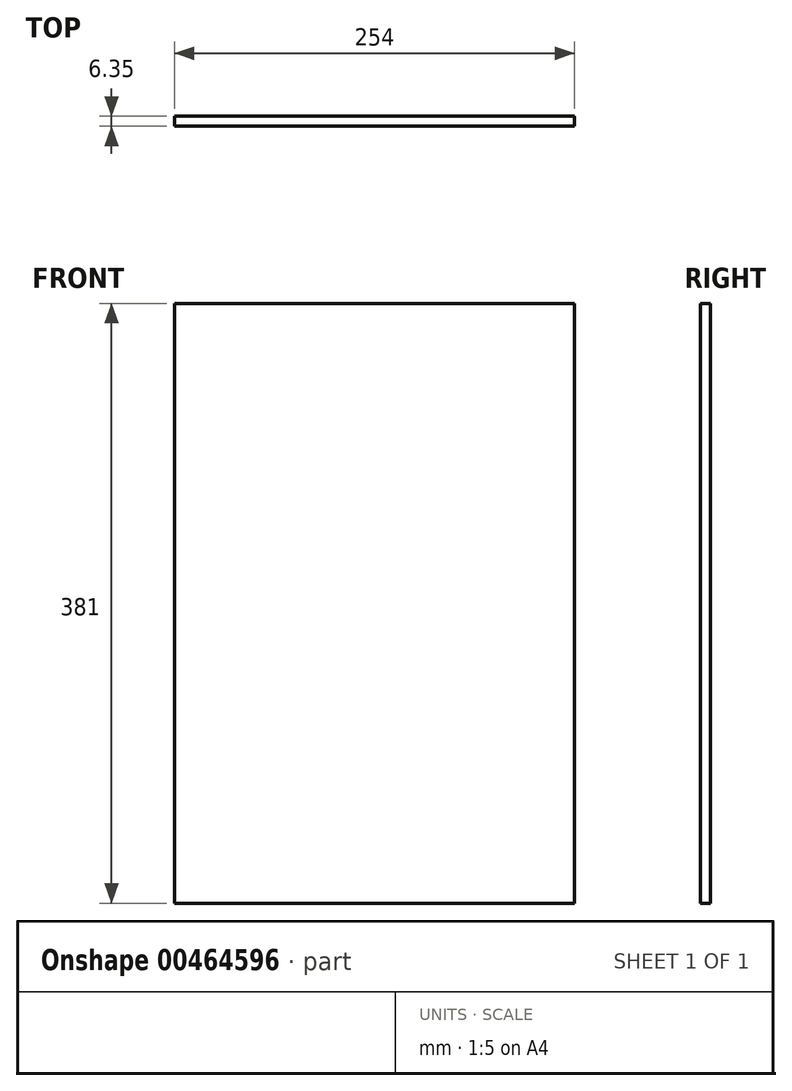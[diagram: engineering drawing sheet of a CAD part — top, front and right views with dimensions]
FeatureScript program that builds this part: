
annotation { "Feature Type Name" : "Feature", "Feature Type Description" : "" }
export const myFeature = defineFeature(function(context is Context, id is Id, definition is map)
    precondition{}
    {
        {
            var Q0;
            Q0=qCreatedBy(makeId("Front.planeOp"),FACE);
            var sketch = newSketch(context, id + "F0", { "sketchPlane" : qUnion([Q0])});
            skLineSegment(sketch, "E0.bottom", {"start": v(-50.4, 326.14) * mm, "end": v(203.6, 326.14) * mm});
            skLineSegment(sketch, "E0.top", {"start": v(-50.4, -54.86) * mm, "end": v(203.6, -54.86) * mm});
            skLineSegment(sketch, "E0.left", {"start": v(-50.4, 326.14) * mm, "end": v(-50.4, -54.86) * mm});
            skLineSegment(sketch, "E0.right", {"start": v(203.6, 326.14) * mm, "end": v(203.6, -54.86) * mm});
            skSolve(sketch);
        }
        {
            var Q0;
            Q0 = qSketchRegion(id + "F0", true);
            extrude(context, id + "F1", {"entities" : qUnion([Q0]), "depth" : 6.35 * mm});
        }
    });
